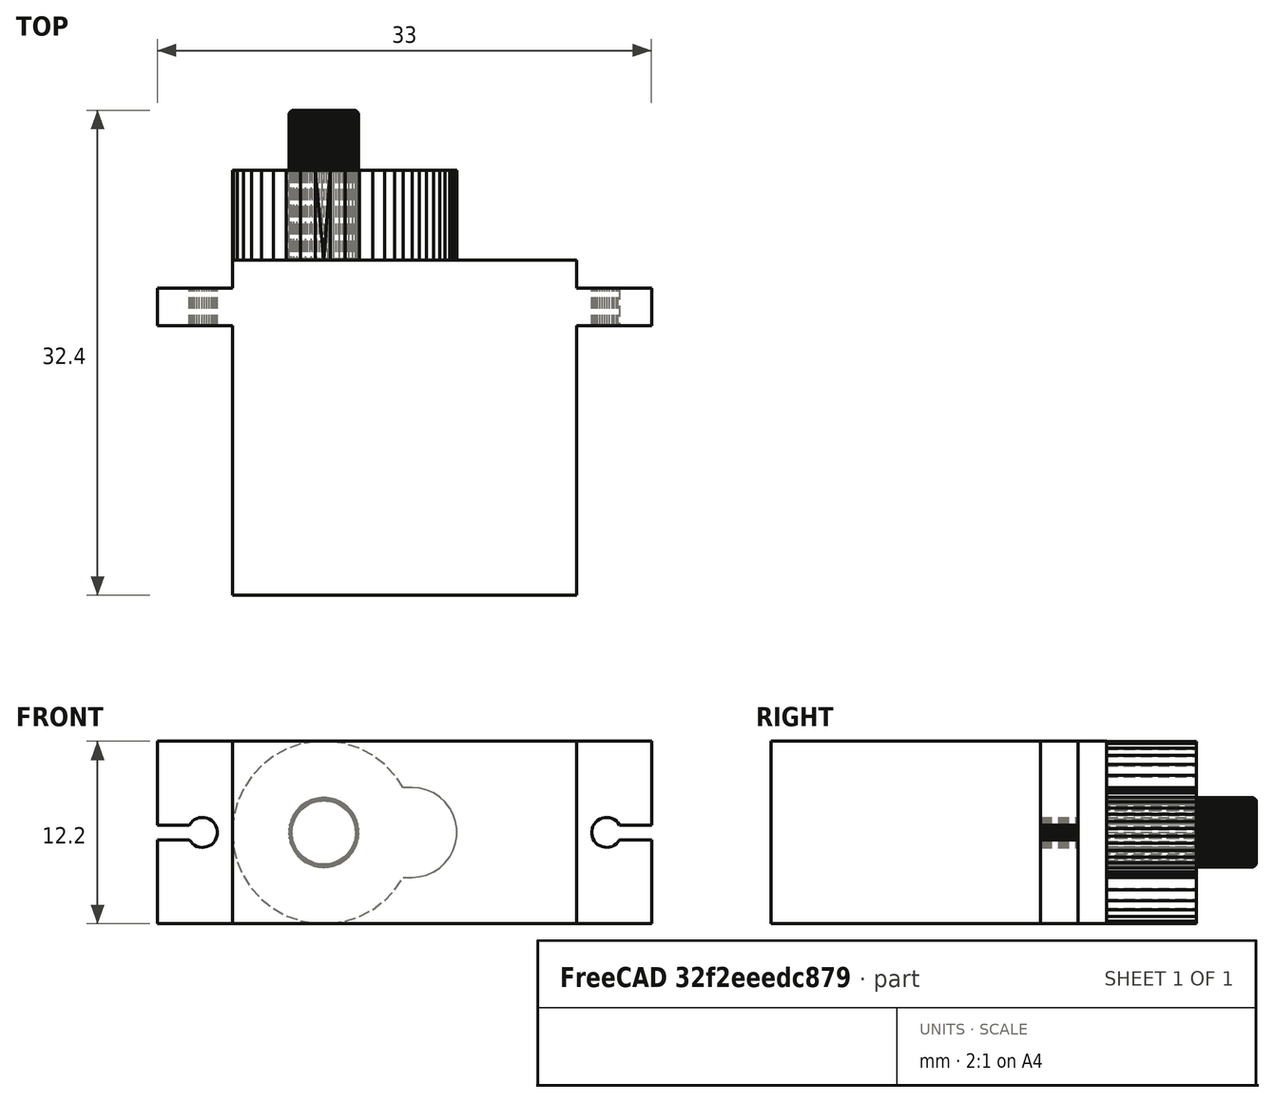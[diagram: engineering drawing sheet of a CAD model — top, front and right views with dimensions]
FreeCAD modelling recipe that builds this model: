
FCSTD DOCUMENT  (FreeCAD 0.20R29177 +426 (Git))
Label: MG90S_servo_refined
License: All rights reserved
LicenseURL: http://en.wikipedia.org/wiki/All_rights_reserved
objects: App::MeasureDistance×9, PartDesign::CoordinateSystem×2, Mesh::Feature×1, Part::Feature×1, Part::Refine×1, PartDesign::FeatureBase×1, Sketcher::SketchObject×1, PartDesign::Body×1
note: 7 computed .brp shape members not serialized (recipe doc carries the construction recipe); baked Part::Feature solids carry a one-line shape summary decoded from their .brp

FEATURE [Mesh::Feature] ImageToStl_com_MG90S  label="ImageToStl.com_MG90S"
FEATURE [Part::Feature] ImageToStl_com_MG90S001
  shape: bbox 33 x 32.4 x 12.2 mm, 2058 faces, 0 solids (baked)
FEATURE [Part::Refine] ImageToStl_com_MG90S001001
  Source = -> ImageToStl_com_MG90S001
FEATURE [App::MeasureDistance] Distance  label="Distance: 4,98 mm"
  Distance = 4.981
  P1 = (466.695,752.809,1601.93)
  P2 = (461.739,752.809,1601.42)
FEATURE [App::MeasureDistance] Distance001  label="Distance: 2,10 mm"
  Distance = 2.10355
  P1 = (466.695,752.809,1597.49)
  P2 = (464.591,752.809,1597.49)
FEATURE [App::MeasureDistance] Distance002  label="Distance: 3,08 mm"
  Distance = 3.07833
  P1 = (466.695,752.809,1595.55)
  P2 = (463.617,752.809,1595.61)
FEATURE [App::MeasureDistance] Distance003  label="Distance: 17,99 mm"
  Distance = 17.9941
  P1 = (461.695,752.809,1603.09)
  P2 = (461.695,734.815,1603.09)
FEATURE [App::MeasureDistance] Distance004  label="Distance: 12,20 mm"
  Distance = 12.2
  P1 = (461.695,734.809,1603.09)
  P2 = (461.695,734.809,1590.89)
FEATURE [App::MeasureDistance] Distance005  label="Distance: 22,96 mm"
  Distance = 22.963
  P1 = (438.732,734.809,1590.94)
  P2 = (461.695,734.809,1590.89)
FEATURE [App::MeasureDistance] Distance006  label="Distance: 1,85 mm"
  Distance = 1.84541
  P1 = (461.786,752.809,1595.51)
  P2 = (463.631,752.809,1595.56)
FEATURE [App::MeasureDistance] Distance007  label="Distance: 1,97 mm"
  Distance = 1.96716
  P1 = (461.782,752.809,1594.87)
  P2 = (463.745,752.809,1594.75)
FEATURE [App::MeasureDistance] Distance008  label="Distance: 2,48 mm"
  Distance = 2.48096
  P1 = (462.797,755.29,1603.09)
  P2 = (462.745,752.809,1603.09)
FEATURE [PartDesign::FeatureBase] BaseFeature
  BaseFeature = -> ImageToStl_com_MG90S001001
FEATURE [PartDesign::CoordinateSystem] LCS_1
  AttacherType = Attacher::AttachEngine3D
  AttachmentOffset = pos=(1,0,0) rot=(0,0,1;0rad)
  MapMode = 45
  Placement = pos=(463.698,752.809,1596.99) rot=(0,0,1;0rad)
  Support = -> [BaseFeature]
FEATURE [PartDesign::CoordinateSystem] LCS_2
  AttacherType = Attacher::AttachEngine3D
  MapMode = 45
  Placement = pos=(444.795,767.209,1596.99) rot=(-1,0,0;1.5708rad)
  Support = -> [BaseFeature]
FEATURE [Sketcher::SketchObject] Sketch
  ExternalGeometry = -> [BaseFeature]
  FullyConstrained = false
  MapMode = 5
  Placement = pos=(0,752.809,0) rot=(1,0,0;1.5708rad)
  Support = -> [BaseFeature]
  sketch-geometry (3):
    g0: GeomPoint X=462.698 Y=1596.99 Z=0
    g1: GeomPoint X=463.698 Y=1596.99 Z=0
    g2: Circle CenterX=463.698 CenterY=1596.99 CenterZ=0 NormalX=0 NormalY=0 NormalZ=1 AngleXU=0 Radius=1.15
  constraints (3):
    c: Symmetric(g-3,g-3,g0)
    c: Coincident(g2,g1)
    c: Diameter(g2) = 2.3
FEATURE [PartDesign::Body] Body
  BaseFeature = -> ImageToStl_com_MG90S001001
  Group = -> [BaseFeature,LCS_1,LCS_2,Sketch]
  Origin = -> Origin
  Tip = -> BaseFeature
